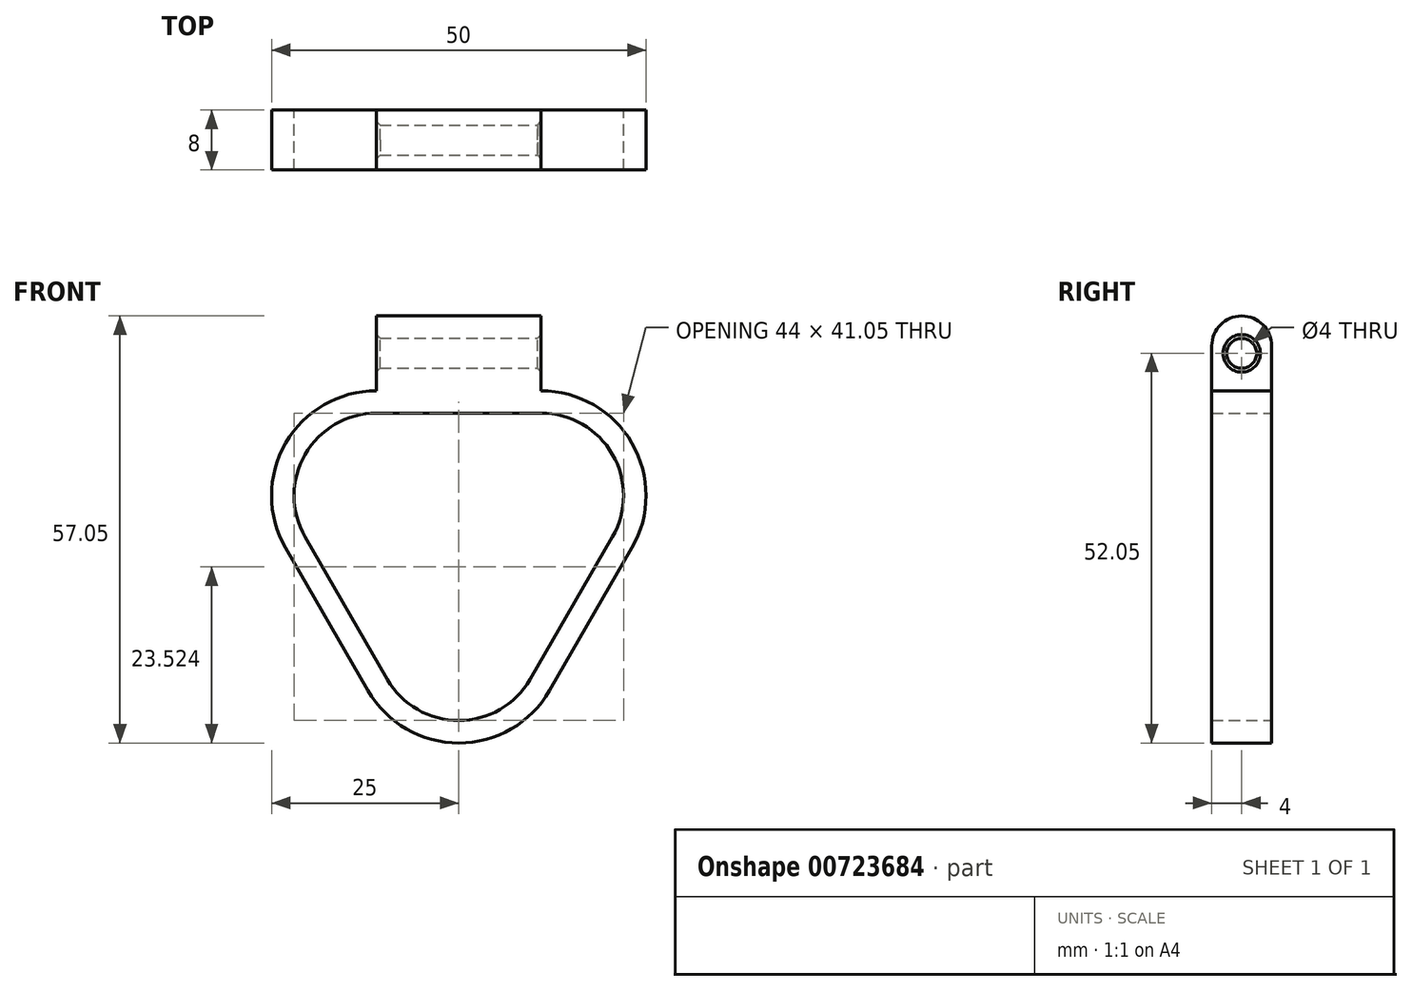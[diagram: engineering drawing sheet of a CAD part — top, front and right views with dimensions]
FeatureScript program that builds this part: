
annotation { "Feature Type Name" : "Feature", "Feature Type Description" : "" }
export const myFeature = defineFeature(function(context is Context, id is Id, definition is map)
    precondition{}
    {
        {
            var Q0;
            Q0=qCreatedBy(makeId("Front.planeOp"),FACE);
            var sketch = newSketch(context, id + "F0", { "sketchPlane" : qUnion([Q0])});
            skCircle(sketch, "E0", {"center": v(0, 0) * mm, "radius": 11 * mm});
            skCircle(sketch, "E1.1.0.0", {"center": v(22, 0) * mm, "radius": 11 * mm});
            skLineSegment(sketch, "E2", {"start": v(0, 11) * mm, "end": v(22, 11) * mm});
            skPoint(sketch, "E3.endSnap0", {"position": v(11, 0) * mm});
            skCircle(sketch, "E4", {"center": v(11, -19.05) * mm, "radius": 11 * mm});
            skLineSegment(sketch, "E5", {"start": v(-9.53, -5.5) * mm, "end": v(1.47, -24.55) * mm});
            skLineSegment(sketch, "E6", {"start": v(31.53, -5.5) * mm, "end": v(20.53, -24.55) * mm});
            skArc(sketch, "E7", {"start": v(-9.53, -5.5) * mm, "mid": v(-9.53, 5.5) * mm, "end": v(0, 11) * mm});
            skArc(sketch, "E8", {"start": v(20.53, -24.55) * mm, "mid": v(11, -30.05) * mm, "end": v(1.47, -24.55) * mm});
            skArc(sketch, "E9", {"start": v(31.53, -5.5) * mm, "mid": v(31.53, 5.5) * mm, "end": v(22, 11) * mm});
            skArc(sketch, "E10.0", {"start": v(-12.12, -7) * mm, "mid": v(-12.12, 7) * mm, "end": v(0, 14) * mm});
            skArc(sketch, "E10.1", {"start": v(34.12, -7) * mm, "mid": v(34.12, 7) * mm, "end": v(22, 14) * mm});
            skLineSegment(sketch, "E10.2", {"start": v(34.12, -7) * mm, "end": v(23.12, -26.05) * mm});
            skLineSegment(sketch, "E10.3", {"start": v(0, 14) * mm, "end": v(22, 14) * mm});
            skArc(sketch, "E10.4", {"start": v(23.12, -26.05) * mm, "mid": v(11, -33.05) * mm, "end": v(-1.12, -26.05) * mm});
            skLineSegment(sketch, "E10.5", {"start": v(-12.12, -7) * mm, "end": v(-1.12, -26.05) * mm});
            skLineSegment(sketch, "E11", {"start": v(33, 0) * mm, "end": v(-11, 0) * mm});
            skLineSegment(sketch, "E12", {"start": v(11, 11) * mm, "end": v(11, -30.05) * mm});
            skSolve(sketch);
        }
        {
            var Q0;
            {var subQ2=sQuery(id+"F0.wireOp",EDGE,"E2");Q0=makeQuery(id+"F0.imprint","IMPRINT",FACE,{"disambiguationData":[TD([[makeQuery(id+"F0.imprint","IMPRINT",EDGE,{"derivedFrom":subQ2}),1.0]])]});}
            extrude(context, id + "F1", {"entities" : qUnion([Q0]), "depth" : 8 * mm, "offsetDistance" : 25.4 * mm});
        }
        {
            var Q0;
            Q0=makeQuery(id+"F1.opExtrude","SWEPT_FACE",FACE,{"disambiguationData":[OSD([sQuery(id+"F0.wireOp",EDGE,"E10.3")])]});
            extrude(context, id + "F2", {"entities" : qUnion([Q0]), "operationType" : NewBodyOperationType.ADD, "depth" : 10 * mm, "offsetDistance" : 25.4 * mm});
        }
        {
            var Q0;
            Q0=makeQuery(id+"F2.opExtrude","SWEPT_FACE",FACE,{"disambiguationData":[OSD([sQuery(id+"F0.wireOp",EDGE,"E10.1"),sQuery(id+"F0.wireOp",EDGE,"E10.3")])]});
            var sketch = newSketch(context, id + "F3", { "sketchPlane" : qUnion([Q0])});
            skCircle(sketch, "E13", {"center": v(-4, 19) * mm, "radius": 1.5 * mm});
            skPoint(sketch, "E13.centerSnap0", {"position": v(-4, 24) * mm});
            skPoint(sketch, "E13.centerSnap1", {"position": v(-8, 19) * mm});
            skSolve(sketch);
        }
        {
            var Q0;
            Q0=makeQuery(id+"F2.opExtrude","SWEPT_FACE",FACE,{"disambiguationData":[OSD([sQuery(id+"F0.wireOp",EDGE,"E10.0"),sQuery(id+"F0.wireOp",EDGE,"E10.3")])]});
            var sketch = newSketch(context, id + "F4", { "sketchPlane" : qUnion([Q0])});
            skCircle(sketch, "E14", {"center": v(4, 19) * mm, "radius": 1.5 * mm});
            skPoint(sketch, "E14.centerSnap0", {"position": v(8, 19) * mm});
            skPoint(sketch, "E14.centerSnap1", {"position": v(4, 24) * mm});
            skSolve(sketch);
        }
        {
            var Q0;
            Q0=sQuery(id+"F3.wireOp",VERTEX,"E13.center");
            var Q1;
            Q1=makeQuery(id+"F1.opExtrude","SWEPT_BODY",BODY,{"disambiguationData":[OSD([sQuery(id+"F0.wireOp",EDGE,"E0"),sQuery(id+"F0.wireOp",EDGE,"E1.1.0.0"),sQuery(id+"F0.wireOp",EDGE,"E2"),sQuery(id+"F0.wireOp",EDGE,"E4"),sQuery(id+"F0.wireOp",EDGE,"E5"),sQuery(id+"F0.wireOp",EDGE,"E6"),sQuery(id+"F0.wireOp",EDGE,"E10.0"),sQuery(id+"F0.wireOp",EDGE,"E10.1"),sQuery(id+"F0.wireOp",EDGE,"E10.2"),sQuery(id+"F0.wireOp",EDGE,"E10.3"),sQuery(id+"F0.wireOp",EDGE,"E10.4"),sQuery(id+"F0.wireOp",EDGE,"E10.5")])]});
            hole(context, id + "F5", {"style" : HoleStyle.C_SINK, "endStyle" : HoleEndStyle.BLIND, "holeDiameter" : 4 * mm, "cSinkDiameter" : 5 * mm, "cSinkAngle" : 90 * degree, "majorDiameter" : 6.35 * mm, "holeDepth" : 12.7 * mm, "isTappedThrough" : true, "tappedDepth" : 12.7 * mm, "tapClearance" : 3, "locations" : qUnion([Q0]), "scope" : qUnion([Q1])});
        }
        {
            var Q0;
            Q0=sQuery(id+"F4.wireOp",VERTEX,"E14.center");
            var Q1;
            Q1=makeQuery(id+"F1.opExtrude","SWEPT_BODY",BODY,{"disambiguationData":[OSD([sQuery(id+"F0.wireOp",EDGE,"E0"),sQuery(id+"F0.wireOp",EDGE,"E1.1.0.0"),sQuery(id+"F0.wireOp",EDGE,"E2"),sQuery(id+"F0.wireOp",EDGE,"E4"),sQuery(id+"F0.wireOp",EDGE,"E5"),sQuery(id+"F0.wireOp",EDGE,"E6"),sQuery(id+"F0.wireOp",EDGE,"E10.0"),sQuery(id+"F0.wireOp",EDGE,"E10.1"),sQuery(id+"F0.wireOp",EDGE,"E10.2"),sQuery(id+"F0.wireOp",EDGE,"E10.3"),sQuery(id+"F0.wireOp",EDGE,"E10.4"),sQuery(id+"F0.wireOp",EDGE,"E10.5")])]});
            hole(context, id + "F6", {"style" : HoleStyle.C_SINK, "endStyle" : HoleEndStyle.BLIND, "holeDiameter" : 4 * mm, "cSinkDiameter" : 5 * mm, "cSinkAngle" : 90 * degree, "majorDiameter" : 6.35 * mm, "holeDepth" : 15 * mm, "isTappedThrough" : true, "tappedDepth" : 12.7 * mm, "tapClearance" : 3, "startFromSketch" : true, "locations" : qUnion([Q0]), "scope" : qUnion([Q1])});
        }
        {
            var Q0;
            {var subQ0=sQuery(id+"F0.wireOp",EDGE,"E10.3");Q0=makeQuery(id+"F2.opExtrude","CAP_EDGE",EDGE,{"disambiguationData":[OSD([subQ0]),TDD([makeQuery(id+"F1.opExtrude","CAP_EDGE",EDGE,{"disambiguationData":[OSD([subQ0])],"isStart":true})])],"isStart":false});}
            var Q1;
            {var subQ0=sQuery(id+"F0.wireOp",EDGE,"E10.3");Q1=makeQuery(id+"F2.opExtrude","CAP_EDGE",EDGE,{"disambiguationData":[OSD([subQ0]),TDD([makeQuery(id+"F1.opExtrude","CAP_EDGE",EDGE,{"disambiguationData":[OSD([subQ0])],"isStart":false})])],"isStart":false});}
            fillet(context, id + "F7", {"entities" : qUnion([Q0, Q1]), "radius" : 4 * mm, "tangentPropagation" : true, "allowEdgeOverflow" : false});
        }
    });
